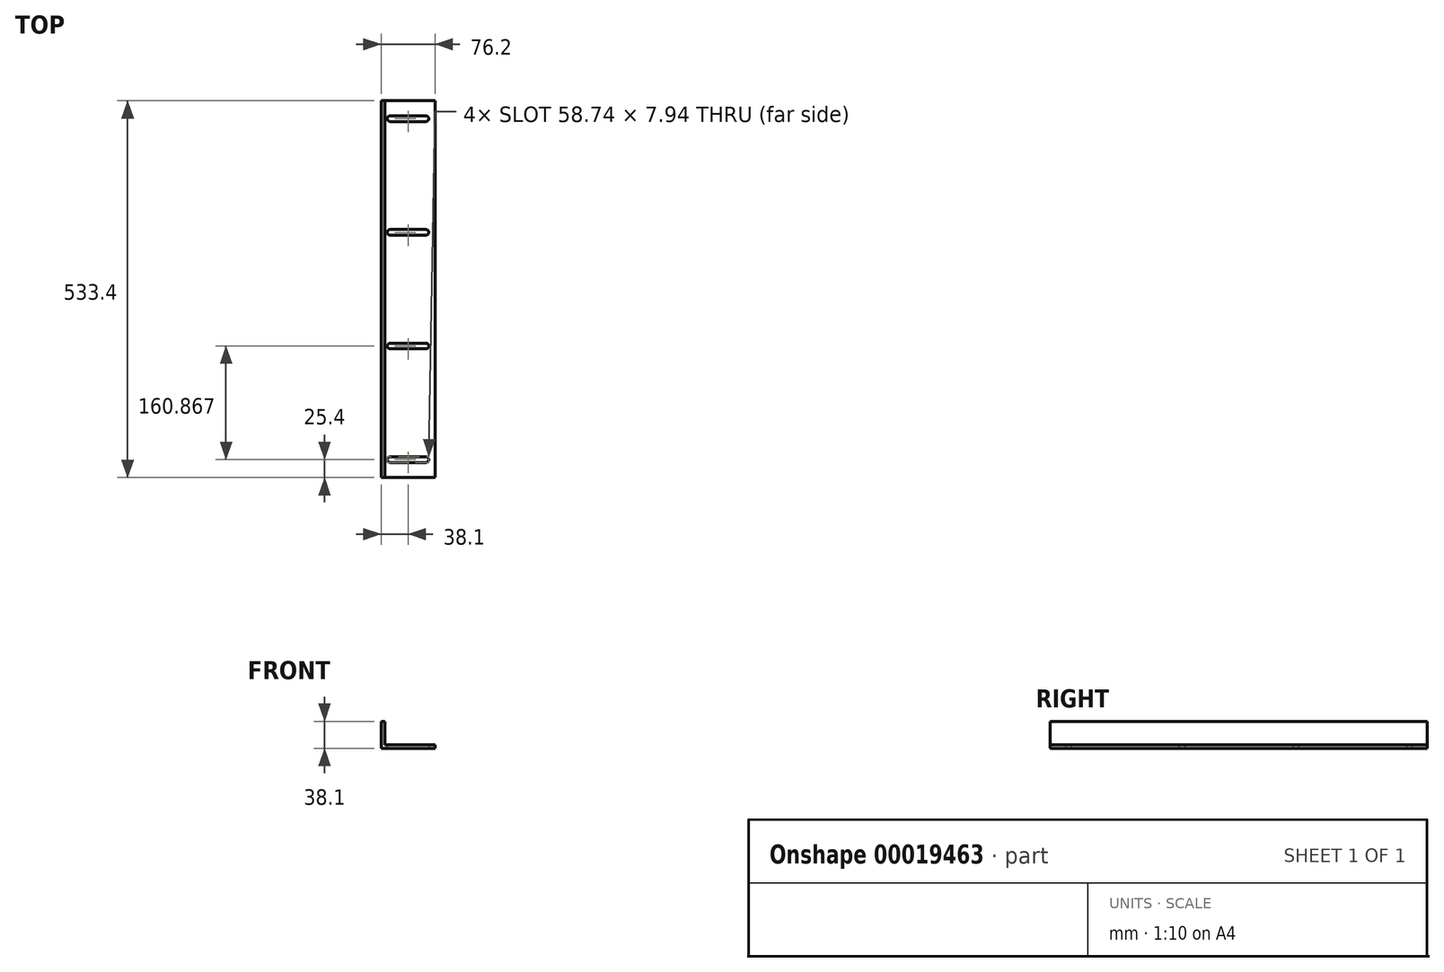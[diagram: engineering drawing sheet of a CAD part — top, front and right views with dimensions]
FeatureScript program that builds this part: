
annotation { "Feature Type Name" : "Feature", "Feature Type Description" : "" }
export const myFeature = defineFeature(function(context is Context, id is Id, definition is map)
    precondition{}
    {
        {
            var Q0;
            Q0=qCreatedBy(makeId("Front.planeOp"),FACE);
            var sketch = newSketch(context, id + "F0", { "sketchPlane" : qUnion([Q0])});
            skLineSegment(sketch, "E0", {"start": v(0, 0) * mm, "end": v(0, 38.1) * mm});
            skLineSegment(sketch, "E1", {"start": v(0, 38.1) * mm, "end": v(5.08, 38.1) * mm});
            skLineSegment(sketch, "E2", {"start": v(5.08, 38.1) * mm, "end": v(5.08, 5.08) * mm});
            skLineSegment(sketch, "E3", {"start": v(5.08, 5.08) * mm, "end": v(76.2, 5.08) * mm});
            skLineSegment(sketch, "E4", {"start": v(76.2, 5.08) * mm, "end": v(76.2, 0) * mm});
            skLineSegment(sketch, "E5", {"start": v(76.2, 0) * mm, "end": v(0, 0) * mm});
            skSolve(sketch);
        }
        {
            var Q0;
            Q0 = qSketchRegion(id + "F0", true);
            extrude(context, id + "F1", {"entities" : qUnion([Q0]), "depth" : 533.4 * mm});
        }
        {
            var Q0;
            Q0=makeQuery(id+"F1.opExtrude","SWEPT_FACE",FACE,{"disambiguationData":[OSD([sQuery(id+"F0.wireOp",EDGE,"E5")])]});
            var sketch = newSketch(context, id + "F2", { "sketchPlane" : qUnion([Q0])});
            skLineSegment(sketch, "E6", {"start": v(63.5, 508) * mm, "end": v(12.7, 508) * mm, "construction": true});
            skLineSegment(sketch, "E7", {"start": v(63.5, 25.4) * mm, "end": v(12.7, 25.4) * mm, "construction": true});
            skLineSegment(sketch, "E8", {"start": v(63.5, 347.13) * mm, "end": v(12.7, 347.13) * mm, "construction": true});
            skLineSegment(sketch, "E9", {"start": v(63.5, 186.27) * mm, "end": v(12.7, 186.27) * mm, "construction": true});
            skCircle(sketch, "E10", {"center": v(63.5, 508) * mm, "radius": 3.97 * mm});
            skCircle(sketch, "E11", {"center": v(12.7, 508) * mm, "radius": 3.97 * mm});
            skCircle(sketch, "E12", {"center": v(63.5, 347.13) * mm, "radius": 3.97 * mm});
            skCircle(sketch, "E13", {"center": v(12.7, 347.13) * mm, "radius": 3.97 * mm});
            skCircle(sketch, "E14", {"center": v(63.5, 186.27) * mm, "radius": 3.97 * mm});
            skCircle(sketch, "E15", {"center": v(12.7, 186.27) * mm, "radius": 3.97 * mm});
            skCircle(sketch, "E16", {"center": v(63.5, 25.4) * mm, "radius": 3.97 * mm});
            skCircle(sketch, "E17", {"center": v(12.7, 25.4) * mm, "radius": 3.97 * mm});
            skLineSegment(sketch, "E18", {"start": v(63.5, 21.43) * mm, "end": v(12.7, 21.43) * mm});
            skLineSegment(sketch, "E19", {"start": v(12.7, 29.37) * mm, "end": v(63.5, 29.37) * mm});
            skLineSegment(sketch, "E20", {"start": v(63.5, 182.3) * mm, "end": v(12.7, 182.3) * mm});
            skLineSegment(sketch, "E21", {"start": v(12.7, 190.24) * mm, "end": v(63.5, 190.24) * mm});
            skLineSegment(sketch, "E22", {"start": v(63.5, 343.16) * mm, "end": v(12.7, 343.16) * mm});
            skLineSegment(sketch, "E23", {"start": v(12.7, 351.1) * mm, "end": v(63.5, 351.1) * mm});
            skLineSegment(sketch, "E24", {"start": v(63.5, 504.03) * mm, "end": v(12.7, 504.03) * mm});
            skLineSegment(sketch, "E25", {"start": v(63.5, 511.97) * mm, "end": v(12.7, 511.97) * mm});
            skSolve(sketch);
        }
        {
            var Q0;
            Q0 = qSketchRegion(id + "F2", true);
            extrude(context, id + "F3", {"entities" : qUnion([Q0]), "operationType" : NewBodyOperationType.REMOVE, "endBound" : BoundingType.THROUGH_ALL, "oppositeDirection" : true, "depth" : 25.4 * mm});
        }
    });
